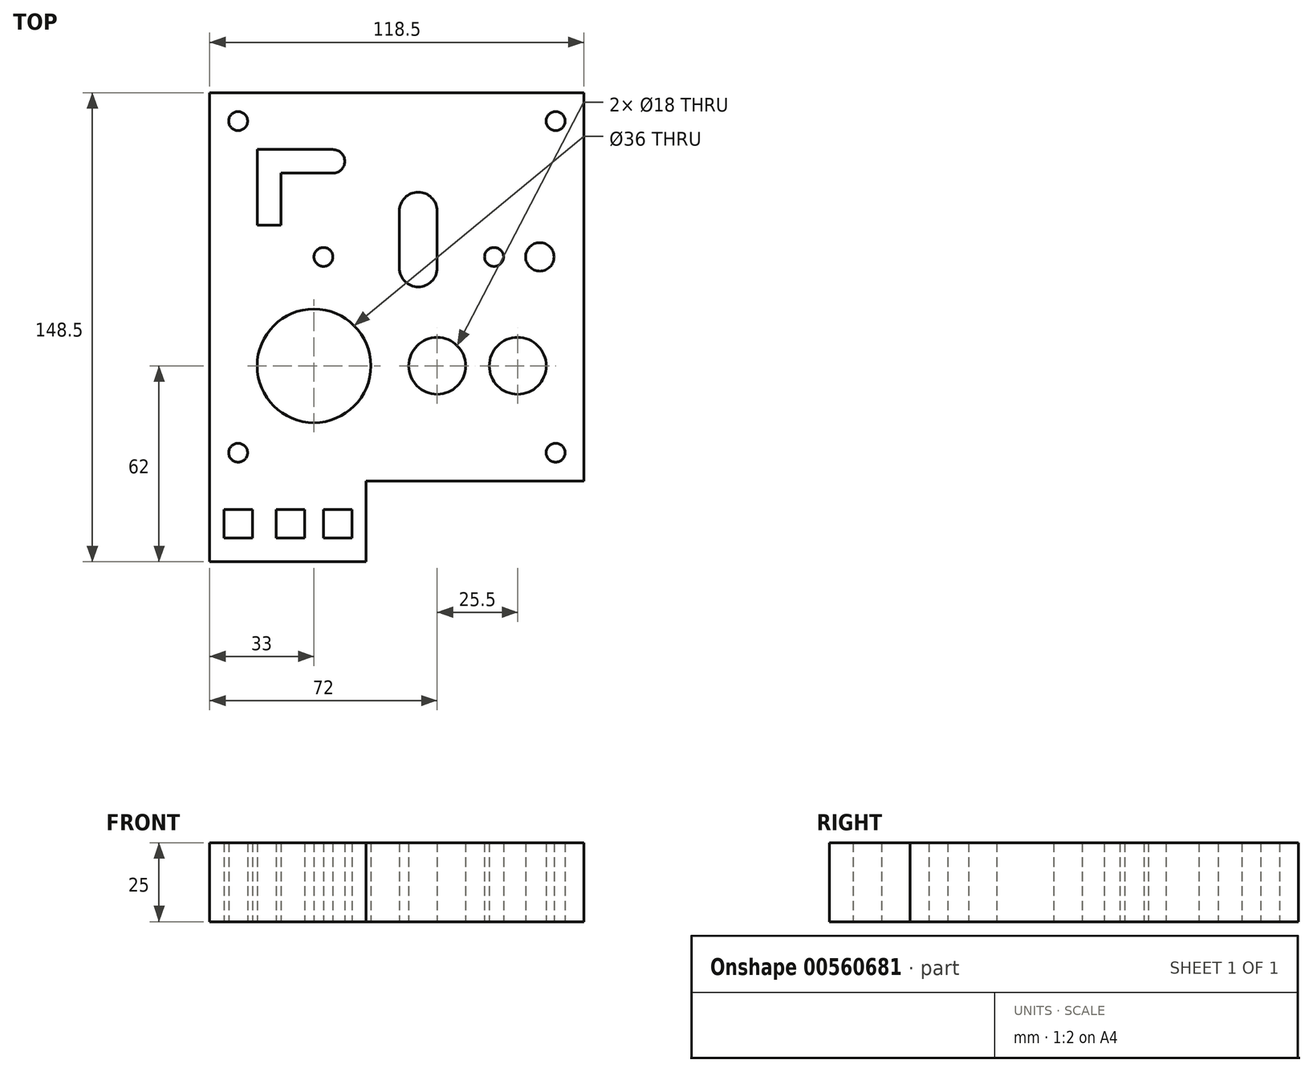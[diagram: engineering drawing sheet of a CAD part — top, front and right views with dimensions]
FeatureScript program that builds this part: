
annotation { "Feature Type Name" : "Feature", "Feature Type Description" : "" }
export const myFeature = defineFeature(function(context is Context, id is Id, definition is map)
    precondition{}
    {
        {
            var Q0;
            Q0=qCreatedBy(makeId("Top.planeOp"),FACE);
            var sketch = newSketch(context, id + "F0", { "sketchPlane" : qUnion([Q0])});
            skLineSegment(sketch, "E0", {"start": v(0, 0) * mm, "end": v(9, 0) * mm});
            skLineSegment(sketch, "E1", {"start": v(0, 0) * mm, "end": v(39, 0) * mm});
            skLineSegment(sketch, "E2", {"start": v(0, 0) * mm, "end": v(0, -9) * mm});
            skCircle(sketch, "E3", {"center": v(9, -9) * mm, "radius": 3 * mm});
            skLineSegment(sketch, "E4", {"start": v(0, 0) * mm, "end": v(0, -18) * mm});
            skLineSegment(sketch, "E5", {"start": v(0, 0) * mm, "end": v(66, 0) * mm});
            skArc(sketch, "E6", {"start": v(39, -25.5) * mm, "mid": v(42.75, -21.75) * mm, "end": v(39, -18) * mm});
            skLineSegment(sketch, "E7", {"start": v(39, -18) * mm, "end": v(15, -18) * mm});
            skLineSegment(sketch, "E8", {"start": v(15, -18) * mm, "end": v(15, -42) * mm});
            skLineSegment(sketch, "E9", {"start": v(15, -42) * mm, "end": v(22.5, -42) * mm});
            skLineSegment(sketch, "E10", {"start": v(22.5, -42) * mm, "end": v(22.5, -25.5) * mm});
            skLineSegment(sketch, "E11", {"start": v(39, -25.5) * mm, "end": v(22.5, -25.5) * mm});
            skArc(sketch, "E12", {"start": v(72, -37.5) * mm, "mid": v(66, -31.5) * mm, "end": v(60, -37.5) * mm});
            skArc(sketch, "E13", {"start": v(60, -55.5) * mm, "mid": v(66, -61.5) * mm, "end": v(72, -55.5) * mm});
            skLineSegment(sketch, "E14", {"start": v(72, -37.5) * mm, "end": v(72, -55.5) * mm});
            skLineSegment(sketch, "E15", {"start": v(60, -55.5) * mm, "end": v(60, -37.5) * mm});
            skLineSegment(sketch, "E16", {"start": v(66, -37.5) * mm, "end": v(66, -31.5) * mm});
            skLineSegment(sketch, "E17", {"start": v(66, 0) * mm, "end": v(90, 0) * mm});
            skLineSegment(sketch, "E18", {"start": v(90, -49) * mm, "end": v(90, -52) * mm});
            skCircle(sketch, "E19", {"center": v(90, -52) * mm, "radius": 3 * mm});
            skLineSegment(sketch, "E20", {"start": v(90, 0) * mm, "end": v(109.5, 0) * mm});
            skLineSegment(sketch, "E21", {"start": v(109.5, 0) * mm, "end": v(118.5, 0) * mm});
            skLineSegment(sketch, "E22", {"start": v(118.5, 0) * mm, "end": v(118.5, -9) * mm});
            skCircle(sketch, "E23", {"center": v(109.5, -9) * mm, "radius": 3 * mm});
            skCircle(sketch, "E24", {"center": v(9, -114) * mm, "radius": 3 * mm});
            skCircle(sketch, "E25", {"center": v(109.5, -114) * mm, "radius": 3 * mm});
            skCircle(sketch, "E26", {"center": v(104.5, -52) * mm, "radius": 4.5 * mm});
            skLineSegment(sketch, "E27", {"start": v(0, -52) * mm, "end": v(36, -52) * mm});
            skCircle(sketch, "E28", {"center": v(36, -52) * mm, "radius": 3 * mm});
            skLineSegment(sketch, "E29", {"start": v(118.5, 0) * mm, "end": v(118.5, -86.5) * mm});
            skCircle(sketch, "E30", {"center": v(97.5, -86.5) * mm, "radius": 9 * mm});
            skCircle(sketch, "E31", {"center": v(72, -86.5) * mm, "radius": 9 * mm});
            skCircle(sketch, "E32", {"center": v(33, -86.5) * mm, "radius": 18 * mm});
            skPoint(sketch, "E33.end.orphan", {"position": v(33, -109.5) * mm});
            skPoint(sketch, "E34.end.orphan", {"position": v(72, -109.5) * mm});
            skPoint(sketch, "E34.start.orphan", {"position": v(97.5, -109.5) * mm});
            skLineSegment(sketch, "E35", {"start": v(33, -86.5) * mm, "end": v(72, -86.5) * mm, "construction": true});
            skLineSegment(sketch, "E36", {"start": v(72, -86.5) * mm, "end": v(97.5, -86.5) * mm, "construction": true});
            skLineSegment(sketch, "E37", {"start": v(97.5, -86.5) * mm, "end": v(109.5, -86.5) * mm, "construction": true});
            skLineSegment(sketch, "E38", {"start": v(118.5, 0) * mm, "end": v(118.5, -123) * mm});
            skLineSegment(sketch, "E39", {"start": v(118.5, -123) * mm, "end": v(49.5, -123) * mm});
            skLineSegment(sketch, "E40", {"start": v(0, 0) * mm, "end": v(0, -148.5) * mm});
            skLineSegment(sketch, "E41", {"start": v(49.5, -148.5) * mm, "end": v(49.5, -123) * mm});
            skLineSegment(sketch, "E42", {"start": v(9, -114) * mm, "end": v(0, -114) * mm});
            skPoint(sketch, "E43.orphan", {"position": v(9, -132) * mm});
            skLineSegment(sketch, "E44", {"start": v(0, -114) * mm, "end": v(0, -132) * mm});
            skLineSegment(sketch, "E45.bottom", {"start": v(4.5, -132) * mm, "end": v(13.5, -132) * mm});
            skLineSegment(sketch, "E45.top", {"start": v(4.5, -141) * mm, "end": v(13.5, -141) * mm});
            skLineSegment(sketch, "E45.left", {"start": v(4.5, -132) * mm, "end": v(4.5, -141) * mm});
            skLineSegment(sketch, "E45.right", {"start": v(13.5, -132) * mm, "end": v(13.5, -141) * mm});
            skLineSegment(sketch, "E46.left", {"start": v(13.5, -132) * mm, "end": v(13.5, -132) * mm});
            skLineSegment(sketch, "E46.right", {"start": v(21, -132) * mm, "end": v(21, -132) * mm});
            skLineSegment(sketch, "E47.bottom", {"start": v(21, -132) * mm, "end": v(30, -132) * mm});
            skLineSegment(sketch, "E47.top", {"start": v(21, -141) * mm, "end": v(30, -141) * mm});
            skLineSegment(sketch, "E47.left", {"start": v(21, -132) * mm, "end": v(21, -141) * mm});
            skLineSegment(sketch, "E47.right", {"start": v(30, -132) * mm, "end": v(30, -141) * mm});
            skLineSegment(sketch, "E48.left", {"start": v(30, -132) * mm, "end": v(30, -132) * mm});
            skLineSegment(sketch, "E48.right", {"start": v(36, -132) * mm, "end": v(36, -132) * mm});
            skLineSegment(sketch, "E49.bottom", {"start": v(36, -132) * mm, "end": v(45, -132) * mm});
            skLineSegment(sketch, "E49.top", {"start": v(36, -141) * mm, "end": v(45, -141) * mm});
            skLineSegment(sketch, "E49.left", {"start": v(36, -132) * mm, "end": v(36, -141) * mm});
            skLineSegment(sketch, "E49.right", {"start": v(45, -132) * mm, "end": v(45, -141) * mm});
            skLineSegment(sketch, "E50", {"start": v(0, -148.5) * mm, "end": v(49.5, -148.5) * mm});
            skLineSegment(sketch, "E51", {"start": v(13.5, -132) * mm, "end": v(21, -132) * mm, "construction": true});
            skLineSegment(sketch, "E52", {"start": v(30, -132) * mm, "end": v(36, -132) * mm, "construction": true});
            skLineSegment(sketch, "E53", {"start": v(4.5, -132) * mm, "end": v(0, -132) * mm, "construction": true});
            skLineSegment(sketch, "E54", {"start": v(39, 0) * mm, "end": v(39, -18) * mm});
            skLineSegment(sketch, "E55", {"start": v(109.5, -114) * mm, "end": v(109.5, -123) * mm});
            skLineSegment(sketch, "E56", {"start": v(109.5, -114) * mm, "end": v(118.5, -114) * mm});
            skLineSegment(sketch, "E57", {"start": v(9, -114) * mm, "end": v(9, -123) * mm});
            skSolve(sketch);
        }
        {
            var Q0;
            Q0 = qSketchRegion(id + "F0", true);
            extrude(context, id + "F1", {"entities" : qUnion([Q0]), "depth" : 25 * mm, "offsetDistance" : 25 * mm});
        }
    });
